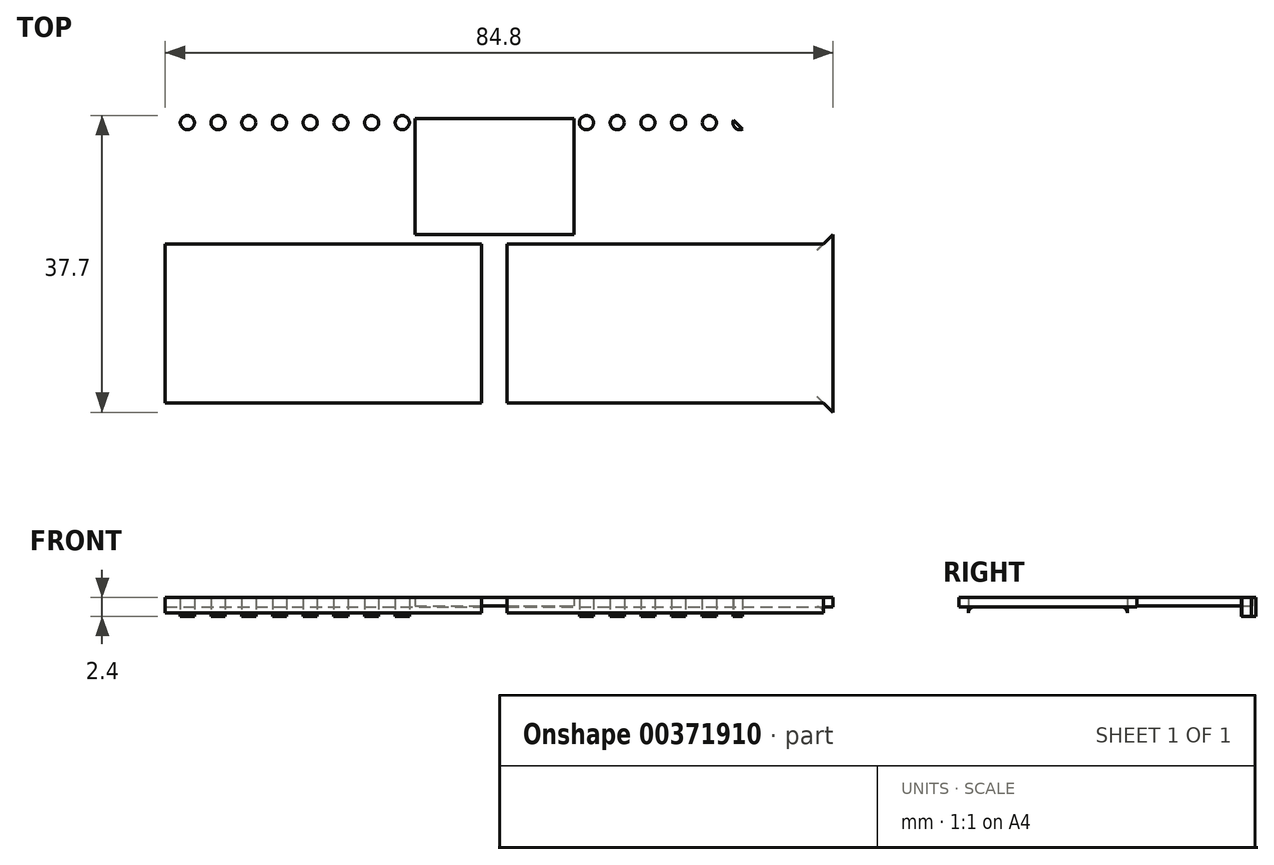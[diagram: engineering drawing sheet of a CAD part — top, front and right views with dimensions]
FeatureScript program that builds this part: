
annotation { "Feature Type Name" : "Feature", "Feature Type Description" : "" }
export const myFeature = defineFeature(function(context is Context, id is Id, definition is map)
    precondition{}
    {
        {
            var Q0;
            Q0=qCreatedBy(makeId("Top.planeOp"),FACE);
            var sketch = newSketch(context, id + "F0", { "sketchPlane" : qUnion([Q0])});
            skLineSegment(sketch, "E0.bottom", {"start": v(-43, 27.2) * mm, "end": v(43, 27.2) * mm});
            skLineSegment(sketch, "E0.top", {"start": v(-43, -27.2) * mm, "end": v(43, -27.2) * mm});
            skLineSegment(sketch, "E0.left", {"start": v(-43, 27.2) * mm, "end": v(-43, -27.2) * mm});
            skLineSegment(sketch, "E0.right", {"start": v(43, 27.2) * mm, "end": v(43, -27.2) * mm});
            skPoint(sketch, "E0.middle", {"position": v(0, 0) * mm});
            skSolve(sketch);
        }
        {
            var Q0;
            Q0 = qSketchRegion(id + "F0", true);
            extrude(context, id + "F1", {"entities" : qUnion([Q0]), "depth" : 2.4 * mm});
        }
        {
            var Q0;
            Q0=makeQuery(id+"F1.opExtrude","CAP_FACE",FACE,{"disambiguationData":[OSD([sQuery(id+"F0.wireOp",EDGE,"E0.bottom"),sQuery(id+"F0.wireOp",EDGE,"E0.top"),sQuery(id+"F0.wireOp",EDGE,"E0.left"),sQuery(id+"F0.wireOp",EDGE,"E0.right")])],"isStart":true});
            var sketch = newSketch(context, id + "F2", { "sketchPlane" : qUnion([Q0])});
            skLineSegment(sketch, "E1.bottom", {"start": v(-88.52, 10.1) * mm, "end": v(88.52, 10.1) * mm});
            skLineSegment(sketch, "E1.top", {"start": v(-88.52, -10.1) * mm, "end": v(88.52, -10.1) * mm});
            skLineSegment(sketch, "E1.left", {"start": v(-88.52, 10.1) * mm, "end": v(-88.52, -10.1) * mm});
            skLineSegment(sketch, "E1.right", {"start": v(88.52, 10.1) * mm, "end": v(88.52, -10.1) * mm});
            skPoint(sketch, "E1.middle", {"position": v(0, 0) * mm});
            skSolve(sketch);
        }
        {
            var Q0;
            Q0 = qSketchRegion(id + "F2", true);
            extrude(context, id + "F3", {"entities" : qUnion([Q0]), "operationType" : NewBodyOperationType.REMOVE, "oppositeDirection" : true, "depth" : 1.2 * mm});
        }
        {
            var Q0;
            Q0=makeQuery(id+"F3.boolean.opBoolean","COPY",FACE,{"derivedFrom":makeQuery(id+"F3.opExtrude","CAP_FACE",FACE,{"disambiguationData":[OSD([sQuery(id+"F2.wireOp",EDGE,"E1.bottom"),sQuery(id+"F2.wireOp",EDGE,"E1.top"),sQuery(id+"F2.wireOp",EDGE,"E1.left"),sQuery(id+"F2.wireOp",EDGE,"E1.right")])],"isStart":false})});
            var sketch = newSketch(context, id + "F4", { "sketchPlane" : qUnion([Q0])});
            skLineSegment(sketch, "E2.bottom", {"start": v(-1.6, 10.1) * mm, "end": v(1.6, 10.1) * mm});
            skLineSegment(sketch, "E2.top", {"start": v(-1.6, -10.1) * mm, "end": v(1.6, -10.1) * mm});
            skLineSegment(sketch, "E2.left", {"start": v(-1.6, 10.1) * mm, "end": v(-1.6, -10.1) * mm});
            skLineSegment(sketch, "E2.right", {"start": v(1.6, 10.1) * mm, "end": v(1.6, -10.1) * mm});
            skPoint(sketch, "E2.middle", {"position": v(0, 0) * mm});
            skSolve(sketch);
        }
        {
            var Q0;
            Q0 = qSketchRegion(id + "F4", true);
            var Q1;
            {var subQ0=sQuery(id+"F0.wireOp",EDGE,"E0.top");var subQ1=sQuery(id+"F0.wireOp",EDGE,"E0.left");var subQ2=sQuery(id+"F0.wireOp",EDGE,"E0.right");Q1=makeQuery(id+"F3.boolean.opBoolean","SPLIT",FACE,{"disambiguationData":[TD([makeQuery(id+"F1.opExtrude","SWEPT_FACE",FACE,{"disambiguationData":[OSD([subQ0])]})])],"derivedFrom":makeQuery(id+"F1.opExtrude","CAP_FACE",FACE,{"disambiguationData":[OSD([sQuery(id+"F0.wireOp",EDGE,"E0.bottom"),subQ0,subQ1,subQ2])],"isStart":true})});}
            extrude(context, id + "F5", {"entities" : qUnion([Q0]), "operationType" : NewBodyOperationType.ADD, "endBound" : BoundingType.UP_TO_SURFACE, "endBoundEntityFace" : qUnion([Q1]), "depth" : 25 * mm});
        }
        {
            var Q0;
            Q0=makeQuery(id+"F1.opExtrude","SWEPT_EDGE",EDGE,{"disambiguationData":[OSD([sQuery(id+"F0.wireOp",EDGE,"E0.top"),sQuery(id+"F0.wireOp",EDGE,"E0.left")])]});
            var Q1;
            Q1=makeQuery(id+"F1.opExtrude","SWEPT_EDGE",EDGE,{"disambiguationData":[OSD([sQuery(id+"F0.wireOp",EDGE,"E0.top"),sQuery(id+"F0.wireOp",EDGE,"E0.right")])]});
            var Q2;
            Q2=makeQuery(id+"F1.opExtrude","SWEPT_EDGE",EDGE,{"disambiguationData":[OSD([sQuery(id+"F0.wireOp",EDGE,"E0.bottom"),sQuery(id+"F0.wireOp",EDGE,"E0.left")])]});
            chamfer(context, id + "F6", {"entities" : qUnion([Q0, Q1, Q2]), "width" : 3 * mm, "tangentPropagation" : true});
        }
        {
            var Q0;
            Q0=makeQuery(id+"F1.opExtrude","SWEPT_EDGE",EDGE,{"disambiguationData":[OSD([sQuery(id+"F0.wireOp",EDGE,"E0.bottom"),sQuery(id+"F0.wireOp",EDGE,"E0.right")])]});
            chamfer(context, id + "F7", {"entities" : qUnion([Q0]), "width" : 14 * mm, "tangentPropagation" : true});
        }
        {
            var Q0;
            {var subQ0=sQuery(id+"F0.wireOp",EDGE,"E0.top");var subQ1=sQuery(id+"F0.wireOp",EDGE,"E0.left");var subQ3=sQuery(id+"F0.wireOp",EDGE,"E0.right");var subQ5=sQuery(id+"F0.wireOp",EDGE,"E0.bottom");var subQ6=makeQuery(id+"F1.opExtrude","CAP_FACE",FACE,{"disambiguationData":[OSD([subQ5,subQ0,subQ1,subQ3])],"isStart":true});Q0=makeQuery(id+"F5.boolean.opBoolean","MERGE",FACE,{"derivedFrom":[makeQuery(id+"F3.boolean.opBoolean","SPLIT",FACE,{"disambiguationData":[TD([makeQuery(id+"F1.opExtrude","SWEPT_FACE",FACE,{"disambiguationData":[OSD([subQ5])]})])],"derivedFrom":subQ6}),makeQuery(id+"F3.boolean.opBoolean","SPLIT",FACE,{"disambiguationData":[TD([makeQuery(id+"F1.opExtrude","SWEPT_FACE",FACE,{"disambiguationData":[OSD([subQ0])]})])],"derivedFrom":subQ6}),makeQuery(id+"F5.opExtrude","CAP_FACE",FACE,{"disambiguationData":[OSD([sQuery(id+"F4.wireOp",EDGE,"E2.bottom"),sQuery(id+"F4.wireOp",EDGE,"E2.top"),sQuery(id+"F4.wireOp",EDGE,"E2.left"),sQuery(id+"F4.wireOp",EDGE,"E2.right")])],"isStart":false})]});}
            var sketch = newSketch(context, id + "F8", { "sketchPlane" : qUnion([Q0])});
            skLineSegment(sketch, "E3.bottom", {"start": v(-10.1, -11.3) * mm, "end": v(10.1, -11.3) * mm});
            skLineSegment(sketch, "E3.top", {"start": v(-10.1, -43.1) * mm, "end": v(10.1, -43.1) * mm});
            skLineSegment(sketch, "E3.left", {"start": v(-10.1, -11.3) * mm, "end": v(-10.1, -43.1) * mm});
            skLineSegment(sketch, "E3.right", {"start": v(10.1, -11.3) * mm, "end": v(10.1, -43.1) * mm});
            skPoint(sketch, "E3.middle", {"position": v(0, -27.2) * mm});
            skSolve(sketch);
        }
        {
            var Q0;
            Q0 = qSketchRegion(id + "F8", true);
            extrude(context, id + "F9", {"entities" : qUnion([Q0]), "operationType" : NewBodyOperationType.REMOVE, "oppositeDirection" : true, "depth" : 1.3 * mm});
        }
        {
            var Q0;
            {var subQ0=sQuery(id+"F2.wireOp",EDGE,"E1.bottom");var subQ1=sQuery(id+"F2.wireOp",EDGE,"E1.top");Q0=makeQuery(id+"F5.boolean.opBoolean","SPLIT",FACE,{"disambiguationData":[TD([makeQuery(id+"F1.opExtrude","SWEPT_FACE",FACE,{"disambiguationData":[OSD([sQuery(id+"F0.wireOp",EDGE,"E0.left")])]})])],"derivedFrom":makeQuery(id+"F3.boolean.opBoolean","COPY",FACE,{"derivedFrom":makeQuery(id+"F3.opExtrude","CAP_FACE",FACE,{"disambiguationData":[OSD([subQ0,subQ1,sQuery(id+"F2.wireOp",EDGE,"E1.left"),sQuery(id+"F2.wireOp",EDGE,"E1.right")])],"isStart":false})})});}
            var sketch = newSketch(context, id + "F10", { "sketchPlane" : qUnion([Q0])});
            skLineSegment(sketch, "E4.bottom", {"start": v(-43, 10.1) * mm, "end": v(-41.8, 10.1) * mm});
            skLineSegment(sketch, "E4.top", {"start": v(-43, -10.1) * mm, "end": v(-41.8, -10.1) * mm});
            skLineSegment(sketch, "E4.left", {"start": v(-43, 10.1) * mm, "end": v(-43, -10.1) * mm});
            skLineSegment(sketch, "E4.right", {"start": v(-41.8, 10.1) * mm, "end": v(-41.8, -10.1) * mm});
            skSolve(sketch);
        }
        {
            var Q0;
            Q0 = qSketchRegion(id + "F10", true);
            extrude(context, id + "F11", {"entities" : qUnion([Q0]), "operationType" : NewBodyOperationType.REMOVE, "oppositeDirection" : true, "depth" : 25 * mm});
        }
        {
            var Q0;
            Q0=makeQuery(id+"F9.boolean.opBoolean","COPY",FACE,{"derivedFrom":makeQuery(id+"F9.opExtrude","CAP_FACE",FACE,{"disambiguationData":[OSD([sQuery(id+"F8.wireOp",EDGE,"E3.bottom"),sQuery(id+"F8.wireOp",EDGE,"E3.top"),sQuery(id+"F8.wireOp",EDGE,"E3.left"),sQuery(id+"F8.wireOp",EDGE,"E3.right")])],"isStart":false})});
            var sketch = newSketch(context, id + "F12", { "sketchPlane" : qUnion([Q0])});
            skLineSegment(sketch, "E5.bottom", {"start": v(-10.1, -27.2) * mm, "end": v(10.1, -27.2) * mm});
            skLineSegment(sketch, "E5.top", {"start": v(-10.1, -26) * mm, "end": v(10.1, -26) * mm});
            skLineSegment(sketch, "E5.left", {"start": v(-10.1, -27.2) * mm, "end": v(-10.1, -26) * mm});
            skLineSegment(sketch, "E5.right", {"start": v(10.1, -27.2) * mm, "end": v(10.1, -26) * mm});
            skSolve(sketch);
        }
        {
            var Q0;
            Q0 = qSketchRegion(id + "F12", true);
            extrude(context, id + "F13", {"entities" : qUnion([Q0]), "operationType" : NewBodyOperationType.REMOVE, "oppositeDirection" : true, "depth" : 25 * mm});
        }
        {
            var Q0;
            Q0=makeQuery(id+"F11.boolean.opBoolean","MERGE",EDGE,{"derivedFrom":[makeQuery(id+"F3.boolean.opBoolean","INTERSECT",EDGE,{"derivedFrom":[makeQuery(id+"F1.opExtrude","SWEPT_FACE",FACE,{"disambiguationData":[OSD([sQuery(id+"F0.wireOp",EDGE,"E0.left")])]}),makeQuery(id+"F3.opExtrude","SWEPT_FACE",FACE,{"disambiguationData":[OSD([sQuery(id+"F2.wireOp",EDGE,"E1.bottom")])]})]}),makeQuery(id+"F11.opExtrude","SWEPT_EDGE",EDGE,{"disambiguationData":[OSD([sQuery(id+"F10.wireOp",EDGE,"E4.bottom"),sQuery(id+"F10.wireOp",EDGE,"E4.left")])]})]});
            var Q1;
            Q1=makeQuery(id+"F11.boolean.opBoolean","MERGE",EDGE,{"derivedFrom":[makeQuery(id+"F3.boolean.opBoolean","INTERSECT",EDGE,{"derivedFrom":[makeQuery(id+"F1.opExtrude","SWEPT_FACE",FACE,{"disambiguationData":[OSD([sQuery(id+"F0.wireOp",EDGE,"E0.left")])]}),makeQuery(id+"F3.opExtrude","SWEPT_FACE",FACE,{"disambiguationData":[OSD([sQuery(id+"F2.wireOp",EDGE,"E1.top")])]})]}),makeQuery(id+"F11.opExtrude","SWEPT_EDGE",EDGE,{"disambiguationData":[OSD([sQuery(id+"F10.wireOp",EDGE,"E4.top"),sQuery(id+"F10.wireOp",EDGE,"E4.left")])]})]});
            var Q2;
            Q2=makeQuery(id+"F13.boolean.opBoolean","MERGE",EDGE,{"derivedFrom":[makeQuery(id+"F9.boolean.opBoolean","INTERSECT",EDGE,{"derivedFrom":[makeQuery(id+"F1.opExtrude","SWEPT_FACE",FACE,{"disambiguationData":[OSD([sQuery(id+"F0.wireOp",EDGE,"E0.bottom")])]}),makeQuery(id+"F9.opExtrude","SWEPT_FACE",FACE,{"disambiguationData":[OSD([sQuery(id+"F8.wireOp",EDGE,"E3.left")])]})]}),makeQuery(id+"F13.opExtrude","SWEPT_EDGE",EDGE,{"disambiguationData":[OSD([sQuery(id+"F12.wireOp",EDGE,"E5.bottom"),sQuery(id+"F12.wireOp",EDGE,"E5.left")])]})]});
            var Q3;
            Q3=makeQuery(id+"F13.boolean.opBoolean","MERGE",EDGE,{"derivedFrom":[makeQuery(id+"F9.boolean.opBoolean","INTERSECT",EDGE,{"derivedFrom":[makeQuery(id+"F1.opExtrude","SWEPT_FACE",FACE,{"disambiguationData":[OSD([sQuery(id+"F0.wireOp",EDGE,"E0.bottom")])]}),makeQuery(id+"F9.opExtrude","SWEPT_FACE",FACE,{"disambiguationData":[OSD([sQuery(id+"F8.wireOp",EDGE,"E3.right")])]})]}),makeQuery(id+"F13.opExtrude","SWEPT_EDGE",EDGE,{"disambiguationData":[OSD([sQuery(id+"F12.wireOp",EDGE,"E5.bottom"),sQuery(id+"F12.wireOp",EDGE,"E5.right")])]})]});
            var Q4;
            Q4=makeQuery(id+"FWoRwIJtC3i9u81_1.1.F11.boolean.opBoolean","MERGE",EDGE,{"derivedFrom":[makeQuery(id+"F3.boolean.opBoolean","INTERSECT",EDGE,{"derivedFrom":[makeQuery(id+"F1.opExtrude","SWEPT_FACE",FACE,{"disambiguationData":[OSD([sQuery(id+"F0.wireOp",EDGE,"E0.right")])]}),makeQuery(id+"F3.opExtrude","SWEPT_FACE",FACE,{"disambiguationData":[OSD([sQuery(id+"F2.wireOp",EDGE,"E1.top")])]})]}),makeQuery(id+"FWoRwIJtC3i9u81_1.1.F11.opExtrude","SWEPT_EDGE",EDGE,{"disambiguationData":[OSD([sQuery(id+"F10.wireOp",EDGE,"E4.top"),sQuery(id+"F10.wireOp",EDGE,"E4.left")])]})]});
            var Q5;
            Q5=makeQuery(id+"FWoRwIJtC3i9u81_1.1.F11.boolean.opBoolean","MERGE",EDGE,{"derivedFrom":[makeQuery(id+"F3.boolean.opBoolean","INTERSECT",EDGE,{"derivedFrom":[makeQuery(id+"F1.opExtrude","SWEPT_FACE",FACE,{"disambiguationData":[OSD([sQuery(id+"F0.wireOp",EDGE,"E0.right")])]}),makeQuery(id+"F3.opExtrude","SWEPT_FACE",FACE,{"disambiguationData":[OSD([sQuery(id+"F2.wireOp",EDGE,"E1.bottom")])]})]}),makeQuery(id+"FWoRwIJtC3i9u81_1.1.F11.opExtrude","SWEPT_EDGE",EDGE,{"disambiguationData":[OSD([sQuery(id+"F10.wireOp",EDGE,"E4.bottom"),sQuery(id+"F10.wireOp",EDGE,"E4.left")])]})]});
            chamfer(context, id + "F14", {"entities" : qUnion([Q0, Q1, Q2, Q3, Q4, Q5]), "width" : 1.2 * mm, "tangentPropagation" : true});
        }
        {
            var Q0;
            {var subQ0=sQuery(id+"F2.wireOp",EDGE,"E1.bottom");Q0=makeQuery(id+"F5.boolean.opBoolean","SPLIT",EDGE,{"disambiguationData":[TD([makeQuery(id+"F1.opExtrude","SWEPT_FACE",FACE,{"disambiguationData":[OSD([sQuery(id+"F0.wireOp",EDGE,"E0.left")])]})])],"derivedFrom":makeQuery(id+"F3.boolean.opBoolean","COPY",EDGE,{"derivedFrom":makeQuery(id+"F3.opExtrude","CAP_EDGE",EDGE,{"disambiguationData":[OSD([subQ0])],"isStart":false})})});}
            var Q1;
            {var subQ0=sQuery(id+"F2.wireOp",EDGE,"E1.top");Q1=makeQuery(id+"F5.boolean.opBoolean","SPLIT",EDGE,{"disambiguationData":[TD([makeQuery(id+"F1.opExtrude","SWEPT_FACE",FACE,{"disambiguationData":[OSD([sQuery(id+"F0.wireOp",EDGE,"E0.left")])]})])],"derivedFrom":makeQuery(id+"F3.boolean.opBoolean","COPY",EDGE,{"derivedFrom":makeQuery(id+"F3.opExtrude","CAP_EDGE",EDGE,{"disambiguationData":[OSD([subQ0])],"isStart":false})})});}
            var Q2;
            Q2=makeQuery(id+"F5.opExtrude","CAP_EDGE",EDGE,{"disambiguationData":[OSD([sQuery(id+"F4.wireOp",EDGE,"E2.left")])],"isStart":true});
            var Q3;
            Q3=makeQuery(id+"F5.opExtrude","CAP_EDGE",EDGE,{"disambiguationData":[OSD([sQuery(id+"F4.wireOp",EDGE,"E2.right")])],"isStart":true});
            var Q4;
            {var subQ0=sQuery(id+"F2.wireOp",EDGE,"E1.bottom");Q4=makeQuery(id+"F5.boolean.opBoolean","SPLIT",EDGE,{"disambiguationData":[TD([makeQuery(id+"F1.opExtrude","SWEPT_FACE",FACE,{"disambiguationData":[OSD([sQuery(id+"F0.wireOp",EDGE,"E0.right")])]})])],"derivedFrom":makeQuery(id+"F3.boolean.opBoolean","COPY",EDGE,{"derivedFrom":makeQuery(id+"F3.opExtrude","CAP_EDGE",EDGE,{"disambiguationData":[OSD([subQ0])],"isStart":false})})});}
            var Q5;
            {var subQ0=sQuery(id+"F2.wireOp",EDGE,"E1.top");Q5=makeQuery(id+"F5.boolean.opBoolean","SPLIT",EDGE,{"disambiguationData":[TD([makeQuery(id+"F1.opExtrude","SWEPT_FACE",FACE,{"disambiguationData":[OSD([sQuery(id+"F0.wireOp",EDGE,"E0.right")])]})])],"derivedFrom":makeQuery(id+"F3.boolean.opBoolean","COPY",EDGE,{"derivedFrom":makeQuery(id+"F3.opExtrude","CAP_EDGE",EDGE,{"disambiguationData":[OSD([subQ0])],"isStart":false})})});}
            fillet(context, id + "F15", {"entities" : qUnion([Q0, Q1, Q2, Q3, Q4, Q5]), "radius" : 0.8 * mm, "tangentPropagation" : true, "allowEdgeOverflow" : false});
        }
        {
            var Q0;
            {var subQ0=sQuery(id+"F0.wireOp",EDGE,"E0.top");var subQ1=sQuery(id+"F0.wireOp",EDGE,"E0.left");var subQ3=sQuery(id+"F0.wireOp",EDGE,"E0.right");var subQ5=sQuery(id+"F0.wireOp",EDGE,"E0.bottom");var subQ6=makeQuery(id+"F1.opExtrude","CAP_FACE",FACE,{"disambiguationData":[OSD([subQ5,subQ0,subQ1,subQ3])],"isStart":true});Q0=makeQuery(id+"F5.boolean.opBoolean","MERGE",FACE,{"derivedFrom":[makeQuery(id+"F3.boolean.opBoolean","SPLIT",FACE,{"disambiguationData":[TD([makeQuery(id+"F1.opExtrude","SWEPT_FACE",FACE,{"disambiguationData":[OSD([subQ5])]})])],"derivedFrom":subQ6}),makeQuery(id+"F3.boolean.opBoolean","SPLIT",FACE,{"disambiguationData":[TD([makeQuery(id+"F1.opExtrude","SWEPT_FACE",FACE,{"disambiguationData":[OSD([subQ0])]})])],"derivedFrom":subQ6}),makeQuery(id+"F5.opExtrude","CAP_FACE",FACE,{"disambiguationData":[OSD([sQuery(id+"F4.wireOp",EDGE,"E2.bottom"),sQuery(id+"F4.wireOp",EDGE,"E2.top"),sQuery(id+"F4.wireOp",EDGE,"E2.left"),sQuery(id+"F4.wireOp",EDGE,"E2.right")])],"isStart":false})]});}
            var sketch = newSketch(context, id + "F16", { "sketchPlane" : qUnion([Q0])});
            skCircle(sketch, "E6", {"center": v(0, 25.5) * mm, "radius": 0.9 * mm});
            skCircle(sketch, "E7.1.0.0", {"center": v(3.9, 25.5) * mm, "radius": 0.9 * mm});
            skCircle(sketch, "E7.2.0.0", {"center": v(7.8, 25.5) * mm, "radius": 0.9 * mm});
            skCircle(sketch, "E7.3.0.0", {"center": v(11.7, 25.5) * mm, "radius": 0.9 * mm});
            skCircle(sketch, "E7.4.0.0", {"center": v(15.6, 25.5) * mm, "radius": 0.9 * mm});
            skCircle(sketch, "E7.5.0.0", {"center": v(19.5, 25.5) * mm, "radius": 0.9 * mm});
            skCircle(sketch, "E7.6.0.0", {"center": v(23.4, 25.5) * mm, "radius": 0.9 * mm});
            skCircle(sketch, "E7.7.0.0", {"center": v(27.3, 25.5) * mm, "radius": 0.9 * mm});
            skCircle(sketch, "E7.8.0.0", {"center": v(31.2, 25.5) * mm, "radius": 0.9 * mm});
            skCircle(sketch, "E7.9.0.0", {"center": v(35.1, 25.5) * mm, "radius": 0.9 * mm});
            skCircle(sketch, "E7.10.0.0", {"center": v(39, 25.5) * mm, "radius": 0.9 * mm});
            skLineSegment(sketch, "E7.direction1", {"start": v(0, 25.5) * mm, "end": v(3.9, 25.5) * mm, "construction": true});
            skCircle(sketch, "E8.1.0.0", {"center": v(-3.9, 25.5) * mm, "radius": 0.9 * mm});
            skCircle(sketch, "E8.2.0.0", {"center": v(-7.8, 25.5) * mm, "radius": 0.9 * mm});
            skCircle(sketch, "E8.3.0.0", {"center": v(-11.7, 25.5) * mm, "radius": 0.9 * mm});
            skCircle(sketch, "E8.4.0.0", {"center": v(-15.6, 25.5) * mm, "radius": 0.9 * mm});
            skCircle(sketch, "E8.5.0.0", {"center": v(-19.5, 25.5) * mm, "radius": 0.9 * mm});
            skCircle(sketch, "E8.6.0.0", {"center": v(-23.4, 25.5) * mm, "radius": 0.9 * mm});
            skCircle(sketch, "E8.7.0.0", {"center": v(-27.3, 25.5) * mm, "radius": 0.9 * mm});
            skCircle(sketch, "E8.8.0.0", {"center": v(-31.2, 25.5) * mm, "radius": 0.9 * mm});
            skCircle(sketch, "E8.9.0.0", {"center": v(-35.1, 25.5) * mm, "radius": 0.9 * mm});
            skCircle(sketch, "E8.10.0.0", {"center": v(-39, 25.5) * mm, "radius": 0.9 * mm});
            skLineSegment(sketch, "E8.direction1", {"start": v(0, 25.5) * mm, "end": v(-3.9, 25.5) * mm, "construction": true});
            skCircle(sketch, "E9.MirrorC", {"center": v(0, -25.5) * mm, "radius": 0.9 * mm});
            skCircle(sketch, "E10.MirrorC", {"center": v(-3.9, -25.5) * mm, "radius": 0.9 * mm});
            skCircle(sketch, "E11.MirrorC", {"center": v(3.9, -25.5) * mm, "radius": 0.9 * mm});
            skCircle(sketch, "E12.MirrorC", {"center": v(39, -25.5) * mm, "radius": 0.9 * mm});
            skCircle(sketch, "E13.MirrorC", {"center": v(35.1, -25.5) * mm, "radius": 0.9 * mm});
            skCircle(sketch, "E14.MirrorC", {"center": v(31.2, -25.5) * mm, "radius": 0.9 * mm});
            skCircle(sketch, "E15.MirrorC", {"center": v(27.3, -25.5) * mm, "radius": 0.9 * mm});
            skCircle(sketch, "E16.MirrorC", {"center": v(23.4, -25.5) * mm, "radius": 0.9 * mm});
            skCircle(sketch, "E17.MirrorC", {"center": v(19.5, -25.5) * mm, "radius": 0.9 * mm});
            skCircle(sketch, "E18.MirrorC", {"center": v(15.6, -25.5) * mm, "radius": 0.9 * mm});
            skCircle(sketch, "E19.MirrorC", {"center": v(11.7, -25.5) * mm, "radius": 0.9 * mm});
            skCircle(sketch, "E20.MirrorC", {"center": v(7.8, -25.5) * mm, "radius": 0.9 * mm});
            skCircle(sketch, "E21.MirrorC", {"center": v(-35.1, -25.5) * mm, "radius": 0.9 * mm});
            skCircle(sketch, "E22.MirrorC", {"center": v(-27.3, -25.5) * mm, "radius": 0.9 * mm});
            skCircle(sketch, "E23.MirrorC", {"center": v(-19.5, -25.5) * mm, "radius": 0.9 * mm});
            skCircle(sketch, "E24.MirrorC", {"center": v(-39, -25.5) * mm, "radius": 0.9 * mm});
            skCircle(sketch, "E25.MirrorC", {"center": v(-31.2, -25.5) * mm, "radius": 0.9 * mm});
            skCircle(sketch, "E26.MirrorC", {"center": v(-23.4, -25.5) * mm, "radius": 0.9 * mm});
            skCircle(sketch, "E27.MirrorC", {"center": v(-7.8, -25.5) * mm, "radius": 0.9 * mm});
            skCircle(sketch, "E28.MirrorC", {"center": v(-11.7, -25.5) * mm, "radius": 0.9 * mm});
            skCircle(sketch, "E29.MirrorC", {"center": v(-15.6, -25.5) * mm, "radius": 0.9 * mm});
            skLineSegment(sketch, "E30.MirrorCS", {"start": v(0, -25.5) * mm, "end": v(-3.9, -25.5) * mm, "construction": true});
            skLineSegment(sketch, "E31.MirrorCS", {"start": v(0, -25.5) * mm, "end": v(3.9, -25.5) * mm, "construction": true});
            skSolve(sketch);
        }
        {
            var Q0;
            Q0=makeQuery(id+"F16.imprint","IMPRINT",FACE,{"disambiguationData":[TD([[makeQuery(id+"F16.imprint","IMPRINT",EDGE,{"derivedFrom":sQuery(id+"F16.wireOp",EDGE,"E6")}),1.0]])]});
            var Q1;
            Q1=makeQuery(id+"F16.imprint","IMPRINT",FACE,{"disambiguationData":[TD([[makeQuery(id+"F16.imprint","IMPRINT",EDGE,{"derivedFrom":sQuery(id+"F16.wireOp",EDGE,"E7.1.0.0")}),1.0]])]});
            var Q2;
            Q2=makeQuery(id+"F16.imprint","IMPRINT",FACE,{"disambiguationData":[TD([[makeQuery(id+"F16.imprint","IMPRINT",EDGE,{"derivedFrom":sQuery(id+"F16.wireOp",EDGE,"E7.2.0.0")}),1.0]])]});
            var Q3;
            Q3=makeQuery(id+"F16.imprint","IMPRINT",FACE,{"disambiguationData":[TD([[makeQuery(id+"F16.imprint","IMPRINT",EDGE,{"derivedFrom":sQuery(id+"F16.wireOp",EDGE,"E7.3.0.0")}),1.0]])]});
            var Q4;
            Q4=makeQuery(id+"F16.imprint","IMPRINT",FACE,{"disambiguationData":[TD([[makeQuery(id+"F16.imprint","IMPRINT",EDGE,{"derivedFrom":sQuery(id+"F16.wireOp",EDGE,"E7.4.0.0")}),1.0]])]});
            var Q5;
            Q5=makeQuery(id+"F16.imprint","IMPRINT",FACE,{"disambiguationData":[TD([[makeQuery(id+"F16.imprint","IMPRINT",EDGE,{"derivedFrom":sQuery(id+"F16.wireOp",EDGE,"E7.5.0.0")}),1.0]])]});
            var Q6;
            Q6=makeQuery(id+"F16.imprint","IMPRINT",FACE,{"disambiguationData":[TD([[makeQuery(id+"F16.imprint","IMPRINT",EDGE,{"derivedFrom":sQuery(id+"F16.wireOp",EDGE,"E7.6.0.0")}),1.0]])]});
            var Q7;
            Q7=makeQuery(id+"F16.imprint","IMPRINT",FACE,{"disambiguationData":[TD([[makeQuery(id+"F16.imprint","IMPRINT",EDGE,{"derivedFrom":sQuery(id+"F16.wireOp",EDGE,"E7.7.0.0")}),1.0]])]});
            var Q8;
            Q8=makeQuery(id+"F16.imprint","IMPRINT",FACE,{"disambiguationData":[TD([[makeQuery(id+"F16.imprint","IMPRINT",EDGE,{"derivedFrom":sQuery(id+"F16.wireOp",EDGE,"E7.8.0.0")}),1.0]])]});
            var Q9;
            Q9=makeQuery(id+"F16.imprint","IMPRINT",FACE,{"disambiguationData":[TD([[makeQuery(id+"F16.imprint","IMPRINT",EDGE,{"derivedFrom":sQuery(id+"F16.wireOp",EDGE,"E7.9.0.0")}),1.0]])]});
            var Q10;
            Q10=makeQuery(id+"F16.imprint","IMPRINT",FACE,{"disambiguationData":[TD([[makeQuery(id+"F16.imprint","IMPRINT",EDGE,{"derivedFrom":sQuery(id+"F16.wireOp",EDGE,"E7.10.0.0")}),1.0]])]});
            var Q11;
            Q11=makeQuery(id+"F16.imprint","IMPRINT",FACE,{"disambiguationData":[TD([[makeQuery(id+"F16.imprint","IMPRINT",EDGE,{"derivedFrom":sQuery(id+"F16.wireOp",EDGE,"E8.1.0.0")}),1.0]])]});
            var Q12;
            Q12=makeQuery(id+"F16.imprint","IMPRINT",FACE,{"disambiguationData":[TD([[makeQuery(id+"F16.imprint","IMPRINT",EDGE,{"derivedFrom":sQuery(id+"F16.wireOp",EDGE,"E8.2.0.0")}),1.0]])]});
            var Q13;
            Q13=makeQuery(id+"F16.imprint","IMPRINT",FACE,{"disambiguationData":[TD([[makeQuery(id+"F16.imprint","IMPRINT",EDGE,{"derivedFrom":sQuery(id+"F16.wireOp",EDGE,"E8.3.0.0")}),1.0]])]});
            var Q14;
            Q14=makeQuery(id+"F16.imprint","IMPRINT",FACE,{"disambiguationData":[TD([[makeQuery(id+"F16.imprint","IMPRINT",EDGE,{"derivedFrom":sQuery(id+"F16.wireOp",EDGE,"E8.4.0.0")}),1.0]])]});
            var Q15;
            Q15=makeQuery(id+"F16.imprint","IMPRINT",FACE,{"disambiguationData":[TD([[makeQuery(id+"F16.imprint","IMPRINT",EDGE,{"derivedFrom":sQuery(id+"F16.wireOp",EDGE,"E8.5.0.0")}),1.0]])]});
            var Q16;
            Q16=makeQuery(id+"F16.imprint","IMPRINT",FACE,{"disambiguationData":[TD([[makeQuery(id+"F16.imprint","IMPRINT",EDGE,{"derivedFrom":sQuery(id+"F16.wireOp",EDGE,"E8.6.0.0")}),1.0]])]});
            var Q17;
            Q17=makeQuery(id+"F16.imprint","IMPRINT",FACE,{"disambiguationData":[TD([[makeQuery(id+"F16.imprint","IMPRINT",EDGE,{"derivedFrom":sQuery(id+"F16.wireOp",EDGE,"E8.7.0.0")}),1.0]])]});
            var Q18;
            Q18=makeQuery(id+"F16.imprint","IMPRINT",FACE,{"disambiguationData":[TD([[makeQuery(id+"F16.imprint","IMPRINT",EDGE,{"derivedFrom":sQuery(id+"F16.wireOp",EDGE,"E8.8.0.0")}),1.0]])]});
            var Q19;
            Q19=makeQuery(id+"F16.imprint","IMPRINT",FACE,{"disambiguationData":[TD([[makeQuery(id+"F16.imprint","IMPRINT",EDGE,{"derivedFrom":sQuery(id+"F16.wireOp",EDGE,"E8.9.0.0")}),1.0]])]});
            var Q20;
            Q20=makeQuery(id+"F16.imprint","IMPRINT",FACE,{"disambiguationData":[TD([[makeQuery(id+"F16.imprint","IMPRINT",EDGE,{"derivedFrom":sQuery(id+"F16.wireOp",EDGE,"E8.10.0.0")}),1.0]])]});
            var Q21;
            Q21=makeQuery(id+"F16.imprint","IMPRINT",FACE,{"disambiguationData":[TD([[makeQuery(id+"F16.imprint","IMPRINT",EDGE,{"derivedFrom":sQuery(id+"F16.wireOp",EDGE,"E16.MirrorC")}),-1.0]])]});
            var Q22;
            Q22=makeQuery(id+"F16.imprint","IMPRINT",FACE,{"disambiguationData":[TD([[makeQuery(id+"F16.imprint","IMPRINT",EDGE,{"derivedFrom":sQuery(id+"F16.wireOp",EDGE,"E25.MirrorC")}),-1.0]])]});
            var Q23;
            Q23=makeQuery(id+"F16.imprint","IMPRINT",FACE,{"disambiguationData":[TD([[makeQuery(id+"F16.imprint","IMPRINT",EDGE,{"derivedFrom":sQuery(id+"F16.wireOp",EDGE,"E15.MirrorC")}),-1.0]])]});
            var Q24;
            Q24=makeQuery(id+"F16.imprint","IMPRINT",FACE,{"disambiguationData":[TD([[makeQuery(id+"F16.imprint","IMPRINT",EDGE,{"derivedFrom":sQuery(id+"F16.wireOp",EDGE,"E17.MirrorC")}),-1.0]])]});
            var Q25;
            Q25=makeQuery(id+"F16.imprint","IMPRINT",FACE,{"disambiguationData":[TD([[makeQuery(id+"F16.imprint","IMPRINT",EDGE,{"derivedFrom":sQuery(id+"F16.wireOp",EDGE,"E22.MirrorC")}),-1.0]])]});
            var Q26;
            Q26=makeQuery(id+"F16.imprint","IMPRINT",FACE,{"disambiguationData":[TD([[makeQuery(id+"F16.imprint","IMPRINT",EDGE,{"derivedFrom":sQuery(id+"F16.wireOp",EDGE,"E24.MirrorC")}),-1.0]])]});
            var Q27;
            Q27=makeQuery(id+"F16.imprint","IMPRINT",FACE,{"disambiguationData":[TD([[makeQuery(id+"F16.imprint","IMPRINT",EDGE,{"derivedFrom":sQuery(id+"F16.wireOp",EDGE,"E26.MirrorC")}),-1.0]])]});
            var Q28;
            Q28=makeQuery(id+"F16.imprint","IMPRINT",FACE,{"disambiguationData":[TD([[makeQuery(id+"F16.imprint","IMPRINT",EDGE,{"derivedFrom":sQuery(id+"F16.wireOp",EDGE,"E23.MirrorC")}),-1.0]])]});
            var Q29;
            Q29=makeQuery(id+"F16.imprint","IMPRINT",FACE,{"disambiguationData":[TD([[makeQuery(id+"F16.imprint","IMPRINT",EDGE,{"derivedFrom":sQuery(id+"F16.wireOp",EDGE,"E18.MirrorC")}),-1.0]])]});
            var Q30;
            Q30=makeQuery(id+"F16.imprint","IMPRINT",FACE,{"disambiguationData":[TD([[makeQuery(id+"F16.imprint","IMPRINT",EDGE,{"derivedFrom":sQuery(id+"F16.wireOp",EDGE,"E19.MirrorC")}),-1.0]])]});
            var Q31;
            Q31=makeQuery(id+"F16.imprint","IMPRINT",FACE,{"disambiguationData":[TD([[makeQuery(id+"F16.imprint","IMPRINT",EDGE,{"derivedFrom":sQuery(id+"F16.wireOp",EDGE,"E21.MirrorC")}),-1.0]])]});
            var Q32;
            Q32=makeQuery(id+"F16.imprint","IMPRINT",FACE,{"disambiguationData":[TD([[makeQuery(id+"F16.imprint","IMPRINT",EDGE,{"derivedFrom":sQuery(id+"F16.wireOp",EDGE,"E29.MirrorC")}),-1.0]])]});
            var Q33;
            Q33=makeQuery(id+"F16.imprint","IMPRINT",FACE,{"disambiguationData":[TD([[makeQuery(id+"F16.imprint","IMPRINT",EDGE,{"derivedFrom":sQuery(id+"F16.wireOp",EDGE,"E28.MirrorC")}),-1.0]])]});
            extrude(context, id + "F17", {"entities" : qUnion([Q0, Q1, Q2, Q3, Q4, Q5, Q6, Q7, Q8, Q9, Q10, Q11, Q12, Q13, Q14, Q15, Q16, Q17, Q18, Q19, Q20, Q21, Q22, Q23, Q24, Q25, Q26, Q27, Q28, Q29, Q30, Q31, Q32, Q33]), "operationType" : NewBodyOperationType.REMOVE, "oppositeDirection" : true, "depth" : 25 * mm});
        }
        {
            var Q0;
            {var subQ0=sQuery(id+"F0.wireOp",EDGE,"E0.top");var subQ1=sQuery(id+"F0.wireOp",EDGE,"E0.left");var subQ3=sQuery(id+"F0.wireOp",EDGE,"E0.right");var subQ5=sQuery(id+"F0.wireOp",EDGE,"E0.bottom");var subQ6=makeQuery(id+"F1.opExtrude","CAP_FACE",FACE,{"disambiguationData":[OSD([subQ5,subQ0,subQ1,subQ3])],"isStart":true});Q0=makeQuery(id+"F5.boolean.opBoolean","MERGE",FACE,{"derivedFrom":[makeQuery(id+"F3.boolean.opBoolean","SPLIT",FACE,{"disambiguationData":[TD([makeQuery(id+"F1.opExtrude","SWEPT_FACE",FACE,{"disambiguationData":[OSD([subQ5])]})])],"derivedFrom":subQ6}),makeQuery(id+"F3.boolean.opBoolean","SPLIT",FACE,{"disambiguationData":[TD([makeQuery(id+"F1.opExtrude","SWEPT_FACE",FACE,{"disambiguationData":[OSD([subQ0])]})])],"derivedFrom":subQ6}),makeQuery(id+"F5.opExtrude","CAP_FACE",FACE,{"disambiguationData":[OSD([sQuery(id+"F4.wireOp",EDGE,"E2.bottom"),sQuery(id+"F4.wireOp",EDGE,"E2.top"),sQuery(id+"F4.wireOp",EDGE,"E2.left"),sQuery(id+"F4.wireOp",EDGE,"E2.right")])],"isStart":false})]});}
            var sketch = newSketch(context, id + "F18", { "sketchPlane" : qUnion([Q0])});
            skCircle(sketch, "E32", {"center": v(-41.3, 0) * mm, "radius": 0.9 * mm});
            skCircle(sketch, "E33.0.1.0", {"center": v(-41.3, 3.9) * mm, "radius": 0.9 * mm});
            skCircle(sketch, "E33.0.2.0", {"center": v(-41.3, 7.8) * mm, "radius": 0.9 * mm});
            skCircle(sketch, "E33.0.3.0", {"center": v(-41.3, 11.7) * mm, "radius": 0.9 * mm});
            skCircle(sketch, "E33.0.4.0", {"center": v(-41.3, 15.6) * mm, "radius": 0.9 * mm});
            skCircle(sketch, "E33.0.5.0", {"center": v(-41.3, 19.5) * mm, "radius": 0.9 * mm});
            skCircle(sketch, "E33.0.6.0", {"center": v(-41.3, 23.4) * mm, "radius": 0.9 * mm});
            skLineSegment(sketch, "E33.direction1", {"start": v(-41.3, 0) * mm, "end": v(-16.3, 0) * mm, "construction": true});
            skLineSegment(sketch, "E33.direction2", {"start": v(-41.3, 0) * mm, "end": v(-41.3, 3.9) * mm, "construction": true});
            skSolve(sketch);
        }
        {
            var Q0;
            Q0=makeQuery(id+"F18.imprint","IMPRINT",FACE,{"disambiguationData":[TD([[makeQuery(id+"F18.imprint","IMPRINT",EDGE,{"derivedFrom":sQuery(id+"F18.wireOp",EDGE,"E33.0.6.0")}),1.0]])]});
            var Q1;
            Q1=makeQuery(id+"F18.imprint","IMPRINT",FACE,{"disambiguationData":[TD([[makeQuery(id+"F18.imprint","IMPRINT",EDGE,{"derivedFrom":sQuery(id+"F18.wireOp",EDGE,"E33.0.5.0")}),1.0]])]});
            var Q2;
            Q2=makeQuery(id+"F18.imprint","IMPRINT",FACE,{"disambiguationData":[TD([[makeQuery(id+"F18.imprint","IMPRINT",EDGE,{"derivedFrom":sQuery(id+"F18.wireOp",EDGE,"E33.0.4.0")}),1.0]])]});
            var Q3;
            Q3=makeQuery(id+"F18.imprint","IMPRINT",FACE,{"disambiguationData":[TD([[makeQuery(id+"F18.imprint","IMPRINT",EDGE,{"derivedFrom":sQuery(id+"F18.wireOp",EDGE,"E33.0.3.0")}),1.0]])]});
            extrude(context, id + "F19", {"entities" : qUnion([Q0, Q1, Q2, Q3]), "operationType" : NewBodyOperationType.REMOVE, "oppositeDirection" : true, "depth" : 25 * mm});
        }
    });
